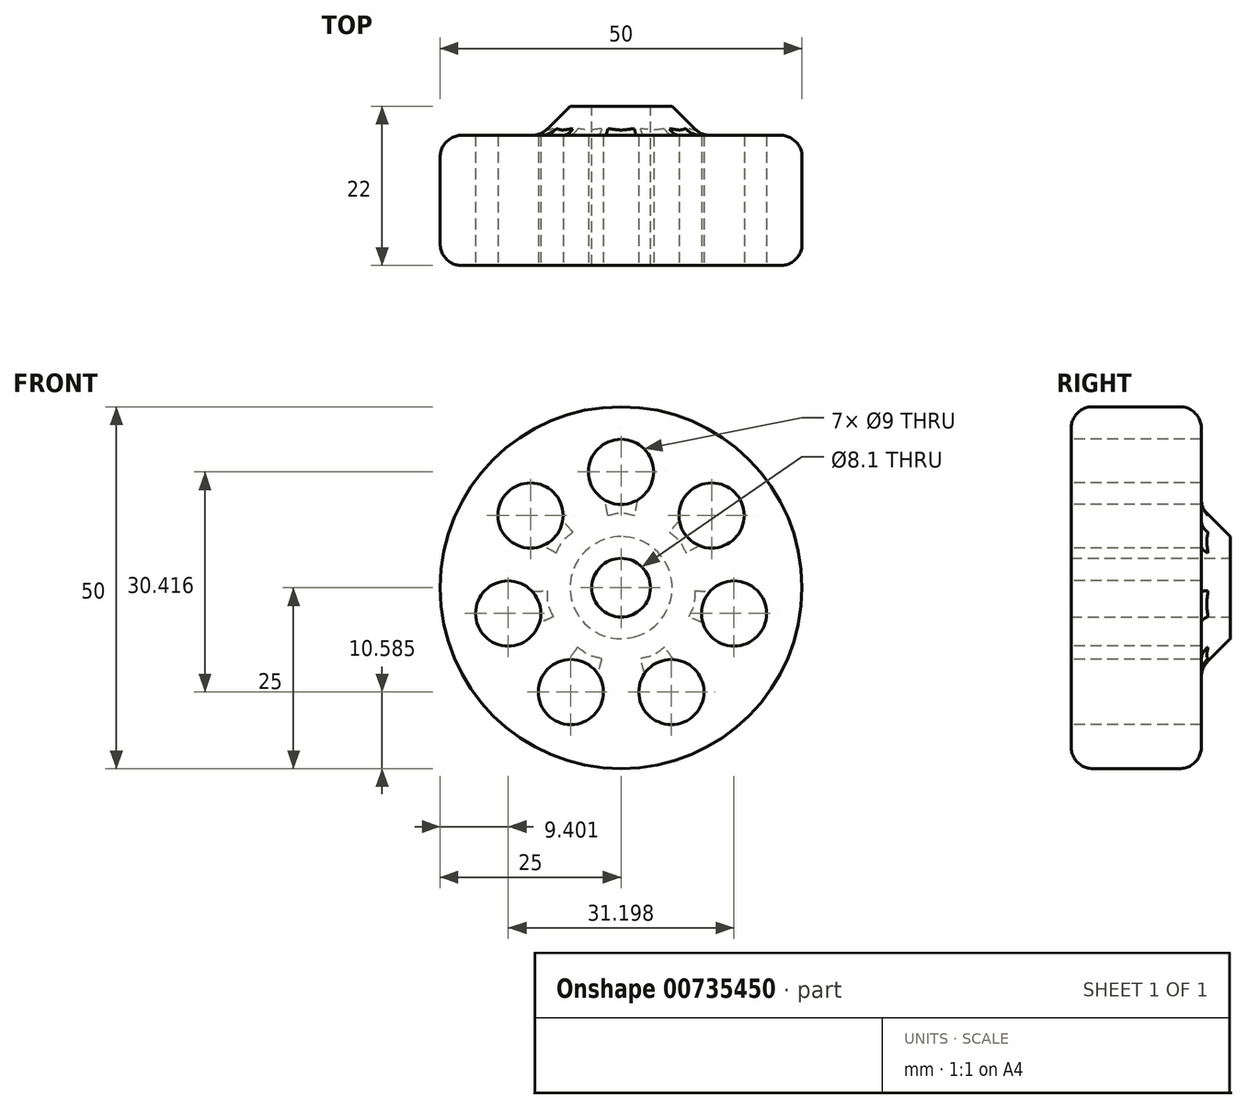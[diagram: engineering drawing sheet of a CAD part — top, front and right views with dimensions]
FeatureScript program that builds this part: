
annotation { "Feature Type Name" : "Feature", "Feature Type Description" : "" }
export const myFeature = defineFeature(function(context is Context, id is Id, definition is map)
    precondition{}
    {
        {
            var Q0;
            Q0=qCreatedBy(makeId("Top.planeOp"),FACE);
            var sketch = newSketch(context, id + "F0", { "sketchPlane" : qUnion([Q0])});
            skLineSegment(sketch, "E0", {"start": v(4.05, 0) * mm, "end": v(4.05, 22) * mm});
            skLineSegment(sketch, "E1", {"start": v(25, 18) * mm, "end": v(25, 0) * mm});
            skLineSegment(sketch, "E2", {"start": v(25, 0) * mm, "end": v(4.05, 0) * mm});
            skLineSegment(sketch, "E3", {"start": v(4.05, 22) * mm, "end": v(7.05, 22) * mm});
            skLineSegment(sketch, "E4", {"start": v(7.05, 22) * mm, "end": v(11.05, 18) * mm});
            skLineSegment(sketch, "E5", {"start": v(11.05, 18) * mm, "end": v(25, 18) * mm});
            skLineSegment(sketch, "E6", {"start": v(0, 52.36) * mm, "end": v(0, -30.18) * mm, "construction": true});
            skSolve(sketch);
        }
        {
            var Q0;
            Q0 = qSketchRegion(id + "F0", true);
            var Q1;
            Q1=sQuery(id+"F0.wireOp",EDGE,"E6");
            revolve(context, id + "F1", {"surfaceOperationType" : NewSurfaceOperationType.NEW, "entities" : qUnion([Q0]), "axis" : qUnion([Q1]), "revolveType" : RevolveType.FULL});
        }
        {
            var Q0;
            Q0=makeQuery(id+"F1.opRevolve","SWEPT_FACE",FACE,{"disambiguationData":[OSD([sQuery(id+"F0.wireOp",EDGE,"E2")])]});
            var sketch = newSketch(context, id + "F2", { "sketchPlane" : qUnion([Q0])});
            skCircle(sketch, "E7", {"center": v(0, 16) * mm, "radius": 4.5 * mm});
            skSolve(sketch);
        }
        {
            var Q0;
            Q0 = qSketchRegion(id + "F2", true);
            extrude(context, id + "F3", {"entities" : qUnion([Q0]), "endBound" : BoundingType.UP_TO_NEXT, "oppositeDirection" : true, "depth" : 25 * mm, "offsetDistance" : 25 * mm});
        }
        {
            var Q0;
            Q0=makeQuery(id+"F3.opExtrude","SWEPT_BODY",BODY,{"disambiguationData":[OSD([sQuery(id+"F2.wireOp",EDGE,"E7")])]});
            var Q1;
            Q1=makeQuery(id+"F1.opRevolve","SWEPT_EDGE",EDGE,{"disambiguationData":[OSD([sQuery(id+"F0.wireOp",EDGE,"E0"),sQuery(id+"F0.wireOp",EDGE,"E3")])]});
            circularPattern(context, id + "F4", {"operationType" : NewBodyOperationType.REMOVE, "entities" : qUnion([Q0]), "axis" : qUnion([Q1]), "angle" : 360 * degree, "instanceCount" : 7, "equalSpace" : true});
        }
        {
            var Q0;
            Q0=makeQuery(id+"F1.opRevolve","SWEPT_EDGE",EDGE,{"disambiguationData":[OSD([sQuery(id+"F0.wireOp",EDGE,"E1"),sQuery(id+"F0.wireOp",EDGE,"E2")])]});
            var Q1;
            Q1=makeQuery(id+"F1.opRevolve","SWEPT_EDGE",EDGE,{"disambiguationData":[OSD([sQuery(id+"F0.wireOp",EDGE,"E1"),sQuery(id+"F0.wireOp",EDGE,"E5")])]});
            var Q2;
            Q2=makeQuery(id+"F1.opRevolve","SWEPT_EDGE",EDGE,{"disambiguationData":[OSD([sQuery(id+"F0.wireOp",EDGE,"E4"),sQuery(id+"F0.wireOp",EDGE,"E5")])]});
            fillet(context, id + "F5", {"entities" : qUnion([Q0, Q1, Q2]), "radius" : 3 * mm, "tangentPropagation" : true, "allowEdgeOverflow" : false});
        }
    });
